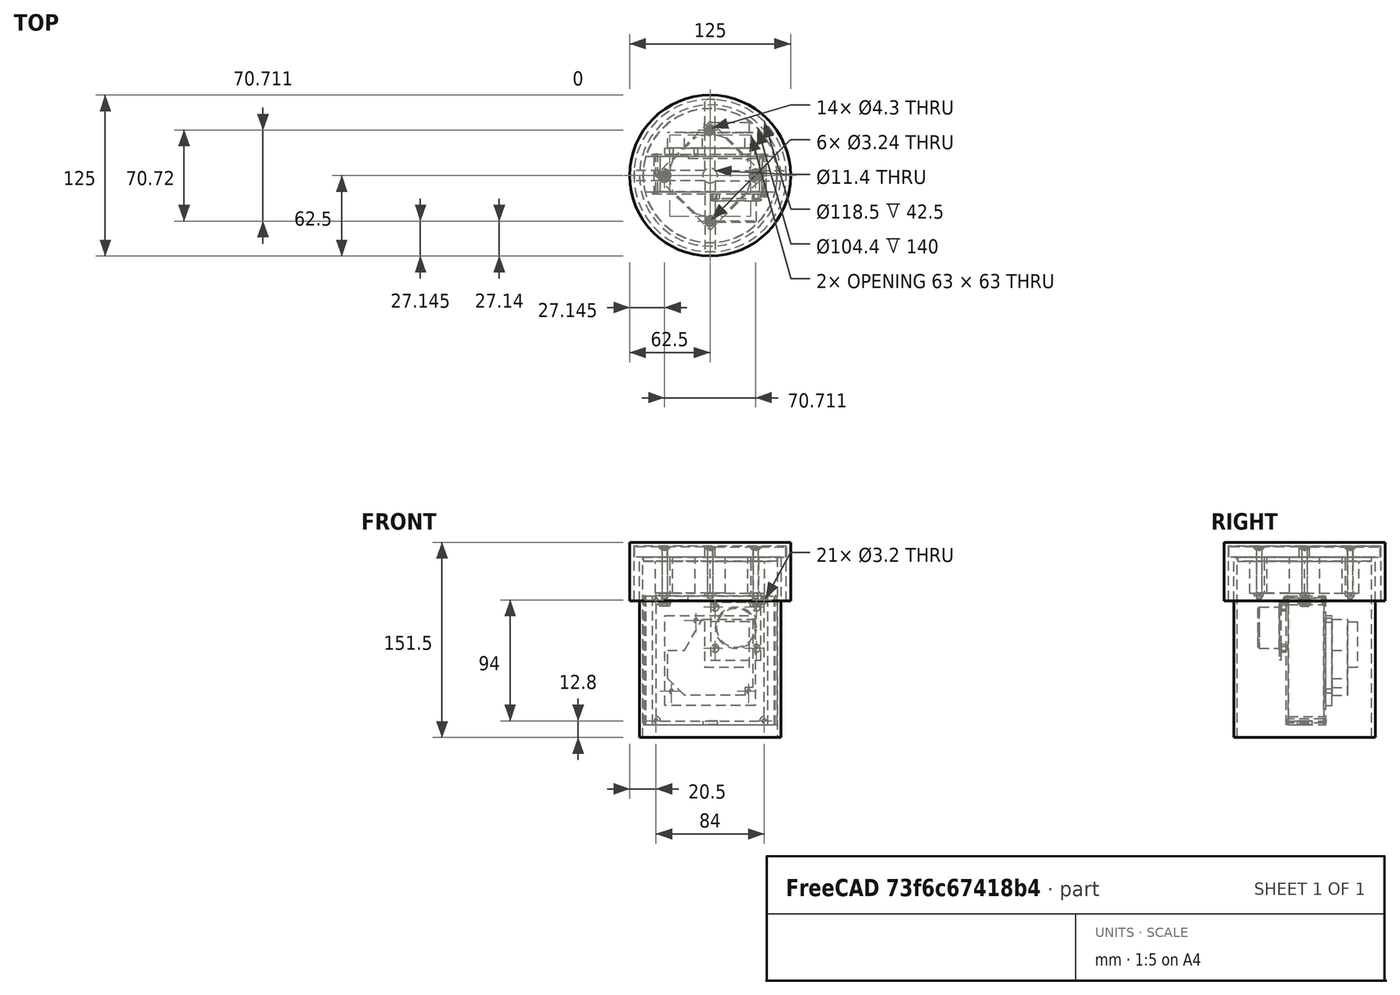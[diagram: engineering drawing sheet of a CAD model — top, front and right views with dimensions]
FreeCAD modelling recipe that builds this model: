
FCSTD DOCUMENT  (FreeCAD 0.18R16117 (Git))
Label: openair
License: All rights reserved
LicenseURL: http://en.wikipedia.org/wiki/All_rights_reserved
objects: Sketcher::SketchObject×20, PartDesign::Pad×15, Part::FeaturePython×14, PartDesign::Body×10, PartDesign::Pocket×5, Mesh::Feature×4, PartDesign::Chamfer×2
note: 86 computed .brp shape members not serialized (recipe doc carries the construction recipe); baked Part::Feature solids carry a one-line shape summary decoded from their .brp

FEATURE [Sketcher::SketchObject] Sketch002  label="tube_body_sketch"
  MapMode = 5
  Support = -> [XY_Plane001]
  sketch-geometry (2):
    g0: Circle CenterX=0 CenterY=0 CenterZ=0 NormalX=0 NormalY=0 NormalZ=1 AngleXU=0 Radius=54.9
    g1: Circle CenterX=0 CenterY=0 CenterZ=0 NormalX=0 NormalY=0 NormalZ=1 AngleXU=0 Radius=52.2
  constraints (4):
    c: Coincident(g0,g-1)
    c: Radius(g0) = 54.9  'tube_outer'
    c: Coincident(g1,g-1)
    c: Radius(g1) = 52.2  'tube_inner'
FEATURE [PartDesign::Pad] Pad001  label="tube_body"
  Length = 140
  Length2 = 100
  Profile = -> Sketch002
  Refine = true
  Reversed = true
  Type = 0
FEATURE [PartDesign::Body] Body001  label="tube"
  Group = -> [Sketch002,Pad001]
  Origin = -> Origin001
  Tip = -> Pad001
FEATURE [Sketcher::SketchObject] Sketch003  label="cross_body_sketch"
  MapMode = 5
  Support = -> [XY_Plane002]
  expr: Constraints[58] = fan_body_sketch.Constraints.hole_center_distance
  expr: Constraints[54] = fan_body_sketch.Constraints.fan_hole_radius
  expr: Constraints[48] = fan_body_sketch.Constraints.fan_hole_radius
  expr: Constraints[57] = fan_body_sketch.Constraints.hole_center_distance
  expr: Constraints[14] = Constraints.cross_width
  expr: Constraints[53] = fan_body_sketch.Constraints.fan_hole_radius
  expr: Constraints[55] = fan_body_sketch.Constraints.fan_hole_radius
  expr: Constraints[56] = fan_body_sketch.Constraints.hole_center_distance
  expr: Constraints[49] = fan_body_sketch.Constraints.hole_center_distance
  expr: Constraints[1] = cap_pocket_sketch.Constraints.cap_inner_radius - 0.2mm
  sketch-geometry (22):
    g0: Circle [constr] CenterX=0 CenterY=0 CenterZ=0 NormalX=0 NormalY=0 NormalZ=1 AngleXU=0 Radius=59.05
    g1: LineSegment [constr] StartX=-4 StartY=-4 StartZ=0 EndX=4 EndY=-4 EndZ=0
    g2: LineSegment [constr] StartX=4 StartY=-4 StartZ=0 EndX=4 EndY=4 EndZ=0
    g3: LineSegment [constr] StartX=4 StartY=4 StartZ=0 EndX=-4 EndY=4 EndZ=0
    g4: LineSegment [constr] StartX=-4 StartY=4 StartZ=0 EndX=-4 EndY=-4 EndZ=0
    g5: LineSegment [constr] StartX=-4 StartY=-4 StartZ=0 EndX=4 EndY=4 EndZ=0
    g6: LineSegment StartX=-4 StartY=4 StartZ=0 EndX=-58.9144 EndY=4 EndZ=0
    g7: LineSegment StartX=-4 StartY=-4 StartZ=0 EndX=-58.9144 EndY=-4 EndZ=0
    g8: LineSegment StartX=-4 StartY=4 StartZ=0 EndX=-4 EndY=58.9144 EndZ=0
    g9: LineSegment StartX=4 StartY=4 StartZ=0 EndX=4 EndY=58.9144 EndZ=0
    g10: LineSegment StartX=4 StartY=4 StartZ=0 EndX=58.9144 EndY=4 EndZ=0
    g11: LineSegment StartX=4 StartY=-4 StartZ=0 EndX=58.9144 EndY=-4 EndZ=0
    g12: LineSegment StartX=-4 StartY=-4 StartZ=0 EndX=-4 EndY=-58.9144 EndZ=0
    g13: LineSegment StartX=4 StartY=-4 StartZ=0 EndX=4 EndY=-58.9144 EndZ=0
    g14: ArcOfCircle CenterX=0 CenterY=0 CenterZ=0 NormalX=0 NormalY=0 NormalZ=1 AngleXU=0 Radius=59.05 StartAngle=4.6446 EndAngle=4.78018
    g15: ArcOfCircle CenterX=0 CenterY=0 CenterZ=0 NormalX=0 NormalY=0 NormalZ=1 AngleXU=0 Radius=59.05 StartAngle=3.0738 EndAngle=3.20938
    g16: ArcOfCircle CenterX=0 CenterY=0 CenterZ=0 NormalX=0 NormalY=0 NormalZ=1 AngleXU=0 Radius=59.05 StartAngle=1.50301 EndAngle=1.63859
    g17: ArcOfCircle CenterX=0 CenterY=0 CenterZ=0 NormalX=0 NormalY=0 NormalZ=1 AngleXU=0 Radius=59.05 StartAngle=6.21539 EndAngle=6.35098
    g18: Circle CenterX=0 CenterY=35.3553 CenterZ=0 NormalX=0 NormalY=0 NormalZ=1 AngleXU=0 Radius=2.15
    g19: Circle CenterX=-35.3553 CenterY=0 CenterZ=0 NormalX=0 NormalY=0 NormalZ=1 AngleXU=0 Radius=2.15
    g20: Circle CenterX=35.3553 CenterY=0 CenterZ=0 NormalX=0 NormalY=0 NormalZ=1 AngleXU=0 Radius=2.15
    g21: Circle CenterX=0 CenterY=-35.3553 CenterZ=0 NormalX=0 NormalY=0 NormalZ=1 AngleXU=0 Radius=2.15
  constraints (59):
    c: Coincident(g0,g-1)
    c: Radius(g0) = 59.05
    c: Coincident(g1,g2)
    c: Coincident(g2,g3)
    c: Coincident(g3,g4)
    c: Coincident(g4,g1)
    c: Horizontal(g1)
    c: Horizontal(g3)
    c: Vertical(g2)
    c: Vertical(g4)
    c: Coincident(g5,g1)
    c: Coincident(g5,g2)
    c: Symmetric(g5,g5,g-1)
    c: DistanceY(g2,g2) = 8  'cross_width'
    c: DistanceX(g3,g3) = 8
    c: Coincident(g6,g3)
    c: PointOnObject(g6,g0)
    c: Horizontal(g6)
    c: Coincident(g7,g1)
    c: Horizontal(g7)
    c: Coincident(g8,g3)
    c: PointOnObject(g8,g0)
    c: Vertical(g8)
    c: Coincident(g9,g2)
    c: Vertical(g9)
    c: Coincident(g10,g2)
    c: PointOnObject(g10,g0)
    c: Horizontal(g10)
    c: Coincident(g11,g1)
    c: Horizontal(g11)
    c: Coincident(g12,g1)
    c: PointOnObject(g12,g0)
    c: Vertical(g12)
    c: Coincident(g13,g1)
    c: Vertical(g13)
    c: Coincident(g14,g-1)
    c: Coincident(g14,g13)
    c: Coincident(g14,g12)
    c: Coincident(g15,g-1)
    c: Coincident(g15,g7)
    c: Coincident(g15,g6)
    c: Coincident(g16,g-1)
    c: Coincident(g16,g8)
    c: Coincident(g16,g9)
    c: Coincident(g17,g-1)
    c: Coincident(g17,g10)
    c: Coincident(g17,g11)
    c: PointOnObject(g18,g-2)
    c: Radius(g18) = 2.15
    c: Distance(g-1,g18) = 35.3553
    c: PointOnObject(g19,g-1)
    c: PointOnObject(g20,g-1)
    c: PointOnObject(g21,g-2)
    c: Radius(g19) = 2.15
    c: Radius(g20) = 2.15
    c: Radius(g21) = 2.15
    c: DistanceX(g19,g-1) = 35.3553
    c: DistanceX(g-1,g20) = 35.3553
    c: DistanceY(g21,g-1) = 35.3553
FEATURE [PartDesign::Pad] Pad002  label="cross_body"
  Length = 8
  Length2 = 100
  Profile = -> Sketch003
  Refine = true
  Type = 0
FEATURE [Sketcher::SketchObject] Sketch004  label="fan_body_sketch"
  MapMode = 5
  Support = -> [XY_Plane003]
  expr: Constraints[57] = Constraints.fan_hole_inset
  expr: Constraints[54] = Constraints.fan_hole_inset
  expr: Constraints[55] = Constraints.fan_hole_inset
  expr: Constraints[53] = Constraints.fan_hole_inset
  expr: Constraints[52] = Constraints.fan_hole_radius
  expr: Constraints[58] = Constraints.fan_hole_inset
  expr: Constraints[51] = Constraints.fan_hole_radius
  expr: Constraints[50] = Constraints.fan_hole_radius
  expr: Constraints[38] = Constraints.fan_cutout_radius
  expr: Constraints[49] = Constraints.fan_hole_inset
  expr: Constraints[37] = Constraints.fan_cutout_radius
  expr: Constraints[56] = Constraints.fan_hole_inset
  expr: Constraints[36] = Constraints.fan_cutout_radius
  expr: Constraints[22] = Constraints.fan_border_thickness
  expr: Constraints[21] = Constraints.fan_border_thickness
  expr: Constraints[20] = Constraints.fan_border_thickness
  expr: Constraints[10] = Constraints.fan_size
  sketch-geometry (20):
    g0: LineSegment StartX=-30 StartY=-30 StartZ=0 EndX=30 EndY=-30 EndZ=0
    g1: LineSegment StartX=30 StartY=-30 StartZ=0 EndX=30 EndY=30 EndZ=0
    g2: LineSegment StartX=30 StartY=30 StartZ=0 EndX=-30 EndY=30 EndZ=0
    g3: LineSegment StartX=-30 StartY=30 StartZ=0 EndX=-30 EndY=-30 EndZ=0
    g4: LineSegment [constr] StartX=-29 StartY=29 StartZ=0 EndX=29 EndY=29 EndZ=0
    g5: LineSegment [constr] StartX=29 StartY=29 StartZ=0 EndX=29 EndY=-29 EndZ=0
    g6: LineSegment [constr] StartX=29 StartY=-29 StartZ=0 EndX=-29 EndY=-29 EndZ=0
    g7: LineSegment [constr] StartX=-29 StartY=-29 StartZ=0 EndX=-29 EndY=29 EndZ=0
    g8: ArcOfCircle CenterX=0 CenterY=0 CenterZ=0 NormalX=0 NormalY=0 NormalZ=1 AngleXU=0 Radius=31.5 StartAngle=1.97189 EndAngle=2.7405
    g9: ArcOfCircle CenterX=0 CenterY=0 CenterZ=0 NormalX=0 NormalY=0 NormalZ=1 AngleXU=0 Radius=31.5 StartAngle=0.401093 EndAngle=1.1697
    g10: ArcOfCircle CenterX=0 CenterY=0 CenterZ=0 NormalX=0 NormalY=0 NormalZ=1 AngleXU=0 Radius=31.5 StartAngle=5.11348 EndAngle=5.88209
    g11: ArcOfCircle CenterX=0 CenterY=0 CenterZ=0 NormalX=0 NormalY=0 NormalZ=1 AngleXU=0 Radius=31.5 StartAngle=3.54269 EndAngle=4.3113
    g12: LineSegment StartX=-29 StartY=-12.2984 StartZ=0 EndX=-29 EndY=12.2984 EndZ=0
    g13: LineSegment StartX=-12.2984 StartY=29 StartZ=0 EndX=12.2984 EndY=29 EndZ=0
    g14: LineSegment StartX=29 StartY=12.2984 StartZ=0 EndX=29 EndY=-12.2984 EndZ=0
    g15: LineSegment StartX=12.2984 StartY=-29 StartZ=0 EndX=-12.2984 EndY=-29 EndZ=0
    g16: Circle CenterX=-25 CenterY=25 CenterZ=0 NormalX=0 NormalY=0 NormalZ=1 AngleXU=0 Radius=2.15
    g17: Circle CenterX=25 CenterY=25 CenterZ=0 NormalX=0 NormalY=0 NormalZ=1 AngleXU=0 Radius=2.15
    g18: Circle CenterX=25 CenterY=-25 CenterZ=0 NormalX=0 NormalY=0 NormalZ=1 AngleXU=0 Radius=2.15
    g19: Circle CenterX=-25 CenterY=-25 CenterZ=0 NormalX=0 NormalY=0 NormalZ=1 AngleXU=0 Radius=2.15
  constraints (60):
    c: Coincident(g0,g1)
    c: Coincident(g1,g2)
    c: Coincident(g2,g3)
    c: Coincident(g3,g0)
    c: Horizontal(g0)
    c: Horizontal(g2)
    c: Vertical(g1)
    c: Vertical(g3)
    c: Symmetric(g1,g0,g-1)
    c: Distance(g1) = 60  'fan_size'
    c: Distance(g0) = 60
    c: Coincident(g4,g5)
    c: Coincident(g5,g6)
    c: Coincident(g6,g7)
    c: Coincident(g7,g4)
    c: Horizontal(g4)
    c: Horizontal(g6)
    c: Vertical(g5)
    c: Vertical(g7)
    c: DistanceX(g2,g4) = 1  'fan_border_thickness'
    c: DistanceX(g4,g1) = 1
    c: DistanceY(g0,g6) = 1
    c: DistanceY(g4,g2) = 1
    c: Coincident(g8,g-1)
    c: PointOnObject(g8,g7)
    c: PointOnObject(g8,g4)
    c: Coincident(g9,g-1)
    c: PointOnObject(g9,g4)
    c: PointOnObject(g9,g5)
    c: Coincident(g10,g-1)
    c: PointOnObject(g10,g5)
    c: PointOnObject(g10,g6)
    c: Coincident(g11,g-1)
    c: PointOnObject(g11,g6)
    c: PointOnObject(g11,g7)
    c: Radius(g8) = 31.5  'fan_cutout_radius'
    c: Radius(g9) = 31.5
    c: Radius(g10) = 31.5
    c: Radius(g11) = 31.5
    c: Coincident(g12,g11)
    c: Coincident(g12,g8)
    c: Coincident(g13,g8)
    c: Coincident(g13,g9)
    c: Coincident(g14,g9)
    c: Coincident(g14,g10)
    c: Coincident(g15,g10)
    c: Coincident(g15,g11)
    c: Radius(g16) = 2.15  'fan_hole_radius'
    c: DistanceX(g2,g16) = 5  'fan_hole_inset'
    c: DistanceY(g16,g2) = 5
    c: Radius(g17) = 2.15
    c: Radius(g18) = 2.15
    c: Radius(g19) = 2.15
    c: DistanceX(g0,g19) = 5
    c: DistanceX(g18,g0) = 5
    c: DistanceX(g17,g1) = 5
    c: DistanceY(g17,g1) = 5
    c: DistanceY(g0,g18) = 5
    c: DistanceY(g0,g19) = 5
    c: Distance(g17,g-1) = 35.3553  'hole_center_distance'
FEATURE [PartDesign::Pad] Pad003  label="fan_body"
  Length = 25
  Length2 = 100
  Profile = -> Sketch004
  Refine = true
  Type = 0
FEATURE [PartDesign::Body] Body003  label="fan"
  Group = -> [Sketch004,Pad003]
  Origin = -> Origin003
  Placement = pos=(0,0,-28) rot=(0,0,1;0.785398rad)
  Tip = -> Pad003
FEATURE [PartDesign::Chamfer] Chamfer  label="cross_countersink"
  Base = -> Pad002 [Edge48,Edge45,Edge39,Edge42]
  BaseFeature = -> Pad002
  Size = 1.61
FEATURE [PartDesign::Body] Body002  label="cross"
  Group = -> [Sketch003,Pad002,Chamfer]
  Origin = -> Origin002
  Tip = -> Chamfer
FEATURE [Sketcher::SketchObject] Sketch005  label="plate_sketch"
  MapMode = 5
  Support = -> [XY_Plane005]
  expr: Constraints[52] = fan_body_sketch.Constraints.fan_hole_radius
  expr: Constraints[51] = fan_body_sketch.Constraints.fan_hole_radius
  expr: Constraints[48] = fan_body_sketch.Constraints.hole_center_distance
  expr: Constraints[49] = fan_body_sketch.Constraints.fan_hole_radius
  expr: Constraints[47] = fan_body_sketch.Constraints.hole_center_distance
  expr: Constraints[50] = fan_body_sketch.Constraints.fan_hole_radius
  expr: Constraints[46] = fan_body_sketch.Constraints.hole_center_distance
  expr: Constraints[45] = fan_body_sketch.Constraints.hole_center_distance
  expr: Constraints[27] = fan_body_sketch.Constraints.fan_cutout_radius
  expr: Constraints[28] = fan_body_sketch.Constraints.fan_cutout_radius
  expr: Constraints[26] = fan_body_sketch.Constraints.fan_cutout_radius
  expr: Constraints[25] = fan_body_sketch.Constraints.fan_cutout_radius
  expr: Constraints[12] = fan_body_sketch.Constraints.fan_size - 2 * fan_body_sketch.Constraints.fan_border_thickness
  expr: Constraints[11] = fan_body_sketch.Constraints.fan_size - 2 * fan_body_sketch.Constraints.fan_border_thickness
  expr: Constraints.diameter = tube_body_sketch.Constraints.tube_inner - 0.2mm
  sketch-geometry (19):
    g0: Circle CenterX=0 CenterY=0 CenterZ=0 NormalX=0 NormalY=0 NormalZ=1 AngleXU=0 Radius=52
    g1: LineSegment [constr] StartX=-29 StartY=29 StartZ=0 EndX=29 EndY=29 EndZ=0
    g2: LineSegment [constr] StartX=29 StartY=29 StartZ=0 EndX=29 EndY=-29 EndZ=0
    g3: LineSegment [constr] StartX=29 StartY=-29 StartZ=0 EndX=-29 EndY=-29 EndZ=0
    g4: LineSegment [constr] StartX=-29 StartY=-29 StartZ=0 EndX=-29 EndY=29 EndZ=0
    g5: ArcOfCircle CenterX=0 CenterY=0 CenterZ=0 NormalX=0 NormalY=0 NormalZ=1 AngleXU=0 Radius=31.5 StartAngle=1.97189 EndAngle=2.7405
    g6: ArcOfCircle CenterX=0 CenterY=0 CenterZ=0 NormalX=0 NormalY=0 NormalZ=1 AngleXU=0 Radius=31.5 StartAngle=0.401093 EndAngle=1.1697
    g7: ArcOfCircle CenterX=0 CenterY=0 CenterZ=0 NormalX=0 NormalY=0 NormalZ=1 AngleXU=0 Radius=31.5 StartAngle=5.11348 EndAngle=5.88209
    g8: ArcOfCircle CenterX=0 CenterY=0 CenterZ=0 NormalX=0 NormalY=0 NormalZ=1 AngleXU=0 Radius=31.5 StartAngle=3.54269 EndAngle=4.3113
    g9: LineSegment StartX=-29 StartY=-12.2984 StartZ=0 EndX=-29 EndY=12.2984 EndZ=0
    g10: LineSegment StartX=-12.2984 StartY=29 StartZ=0 EndX=12.2984 EndY=29 EndZ=0
    g11: LineSegment StartX=29 StartY=12.2984 StartZ=0 EndX=29 EndY=-12.2984 EndZ=0
    g12: LineSegment StartX=12.2984 StartY=-29 StartZ=0 EndX=-12.2984 EndY=-29 EndZ=0
    g13: LineSegment [constr] StartX=-29 StartY=29 StartZ=0 EndX=29 EndY=-29 EndZ=0
    g14: LineSegment [constr] StartX=29 StartY=29 StartZ=0 EndX=-29 EndY=-29 EndZ=0
    g15: Circle CenterX=-25 CenterY=25 CenterZ=0 NormalX=0 NormalY=0 NormalZ=1 AngleXU=0 Radius=2.15
    g16: Circle CenterX=25 CenterY=25 CenterZ=0 NormalX=0 NormalY=0 NormalZ=1 AngleXU=0 Radius=2.15
    g17: Circle CenterX=25 CenterY=-25 CenterZ=0 NormalX=0 NormalY=0 NormalZ=1 AngleXU=0 Radius=2.15
    g18: Circle CenterX=-25 CenterY=-25 CenterZ=0 NormalX=0 NormalY=0 NormalZ=1 AngleXU=0 Radius=2.15
  constraints (53):
    c: Coincident(g0,g-1)
    c: Radius(g0) = 52  'diameter'
    c: Coincident(g1,g2)
    c: Coincident(g2,g3)
    c: Coincident(g3,g4)
    c: Coincident(g4,g1)
    c: Horizontal(g1)
    c: Horizontal(g3)
    c: Vertical(g2)
    c: Vertical(g4)
    c: Symmetric(g3,g1,g-1)
    c: Distance(g1) = 58
    c: Distance(g4) = 58
    c: Coincident(g5,g-1)
    c: PointOnObject(g5,g4)
    c: PointOnObject(g5,g1)
    c: Coincident(g6,g-1)
    c: PointOnObject(g6,g1)
    c: PointOnObject(g6,g2)
    c: Coincident(g7,g-1)
    c: PointOnObject(g7,g2)
    c: PointOnObject(g7,g3)
    c: Coincident(g8,g-1)
    c: PointOnObject(g8,g3)
    c: PointOnObject(g8,g4)
    c: Radius(g5) = 31.5
    c: Radius(g6) = 31.5
    c: Radius(g7) = 31.5
    c: Radius(g8) = 31.5
    c: Coincident(g9,g8)
    c: Coincident(g9,g5)
    c: Coincident(g10,g5)
    c: Coincident(g10,g6)
    c: Coincident(g11,g6)
    c: Coincident(g11,g7)
    c: Coincident(g12,g7)
    c: Coincident(g12,g8)
    c: Coincident(g13,g1)
    c: Coincident(g13,g2)
    c: Coincident(g14,g1)
    c: Coincident(g14,g3)
    c: PointOnObject(g15,g13)
    c: PointOnObject(g16,g14)
    c: PointOnObject(g17,g13)
    c: PointOnObject(g18,g14)
    c: Distance(g15,g-1) = 35.3553
    c: Distance(g16,g-1) = 35.3553
    c: Distance(g17,g-1) = 35.3553
    c: Distance(g-1,g18) = 35.3553
    c: Radius(g15) = 2.15
    c: Radius(g16) = 2.15
    c: Radius(g18) = 2.15
    c: Radius(g17) = 2.15
FEATURE [PartDesign::Pad] Pad004  label="plate_body"
  Length = 3
  Length2 = 100
  Profile = -> Sketch005
  Refine = true
  Type = 0
FEATURE [PartDesign::Body] Body005  label="plate"
  Group = -> [Sketch005,Pad004]
  Origin = -> Origin005
  Placement = pos=(0,0,-3) rot=(0,0,1;0.785398rad)
  Tip = -> Pad004
FEATURE [Sketcher::SketchObject] Sketch006  label="housing_body_sketch"
  MapMode = 5
  Support = -> [XY_Plane006]
  expr: Constraints[1] = tube_body_sketch.Constraints.tube_inner - 0.2mm
  sketch-geometry (5):
    g0: Circle [constr] CenterX=0 CenterY=0 CenterZ=0 NormalX=0 NormalY=0 NormalZ=1 AngleXU=0 Radius=52
    g1: LineSegment StartX=-49.7896 StartY=15 StartZ=0 EndX=49.7896 EndY=15 EndZ=0
    g2: LineSegment StartX=-50.4752 StartY=-12.5 StartZ=0 EndX=50.4752 EndY=-12.5 EndZ=0
    g3: ArcOfCircle CenterX=0 CenterY=0 CenterZ=0 NormalX=0 NormalY=0 NormalZ=1 AngleXU=0 Radius=52 StartAngle=6.04042 EndAngle=6.5758
    g4: ArcOfCircle CenterX=0 CenterY=0 CenterZ=0 NormalX=0 NormalY=0 NormalZ=1 AngleXU=0 Radius=52 StartAngle=2.84897 EndAngle=3.38435
  constraints (14):
    c: Coincident(g0,g-1)
    c: Radius(g0) = 52
    c: Horizontal(g1)
    c: Horizontal(g2)
    c: Coincident(g3,g-1)
    c: Coincident(g3,g1)
    c: Coincident(g3,g2)
    c: Coincident(g4,g-1)
    c: Coincident(g4,g2)
    c: Coincident(g4,g1)
    c: DistanceY(g3,g1) = 15  'housing_depth_back'
    c: DistanceY(g2,g3) = 12.5  'housing_depth_front'
    c: Equal(g3,g0)
    c: Equal(g4,g0)
FEATURE [PartDesign::Pad] Pad005  label="housing_body"
  Length = 100
  Length2 = 100
  Profile = -> Sketch006
  Refine = true
  Type = 0
FEATURE [Sketcher::SketchObject] Sketch007  label="housing_cutouts_sketch"
  ExternalGeometry = -> [Pad005]
  MapMode = 5
  Placement = pos=(0,-12.5,0) rot=(1,0,0;1.5708rad)
  Support = -> [Pad005]
  expr: Constraints[61] = Constraints.housing_hole_keep_radius
  expr: Constraints[60] = Constraints.housing_hole_keep_radius
  expr: Constraints[43] = Constraints.housing_hole_radius
  expr: Constraints[42] = Constraints.housing_hole_radius
  expr: Constraints[59] = Constraints.housing_hole_keep_radius
  expr: Constraints[49] = Constraints.housing_hole_radius
  expr: Constraints[37] = Constraints.cutout_inset
  expr: Constraints[36] = Constraints.module_hole_inset
  expr: Constraints[24] = Constraints.cutout_inset
  expr: Constraints[35] = Constraints.module_hole_inset
  expr: Constraints[23] = Constraints.cutout_inset
  expr: Constraints[34] = Constraints.module_hole_inset
  sketch-geometry (26):
    g0: LineSegment [constr] StartX=-45 StartY=100 StartZ=0 EndX=45 EndY=100 EndZ=0
    g1: LineSegment [constr] StartX=45 StartY=100 StartZ=0 EndX=45 EndY=0 EndZ=0
    g2: LineSegment [constr] StartX=45 StartY=0 StartZ=0 EndX=-45 EndY=0 EndZ=0
    g3: LineSegment [constr] StartX=-45 StartY=0 StartZ=0 EndX=-45 EndY=100 EndZ=0
    g4: LineSegment [constr] StartX=-50.4752 StartY=100 StartZ=0 EndX=50.4752 EndY=0 EndZ=0
    g5: GeomPoint X=0 Y=50 Z=0
    g6: LineSegment [constr] StartX=-44 StartY=99 StartZ=0 EndX=44 EndY=99 EndZ=0
    g7: LineSegment [constr] StartX=44 StartY=99 StartZ=0 EndX=44 EndY=1 EndZ=0
    g8: LineSegment [constr] StartX=44 StartY=1 StartZ=0 EndX=-44 EndY=1 EndZ=0
    g9: LineSegment [constr] StartX=-44 StartY=1 StartZ=0 EndX=-44 EndY=99 EndZ=0
    g10: LineSegment [constr] StartX=-42 StartY=97 StartZ=0 EndX=42 EndY=97 EndZ=0
    g11: LineSegment [constr] StartX=42 StartY=97 StartZ=0 EndX=42 EndY=3 EndZ=0
    g12: LineSegment [constr] StartX=42 StartY=3 StartZ=0 EndX=-42 EndY=3 EndZ=0
    g13: LineSegment [constr] StartX=-42 StartY=3 StartZ=0 EndX=-42 EndY=97 EndZ=0
    g14: Circle CenterX=-42 CenterY=97 CenterZ=0 NormalX=0 NormalY=0 NormalZ=1 AngleXU=0 Radius=1.6
    g15: Circle CenterX=42 CenterY=97 CenterZ=0 NormalX=0 NormalY=0 NormalZ=1 AngleXU=0 Radius=1.6
    g16: Circle CenterX=42 CenterY=3 CenterZ=0 NormalX=0 NormalY=0 NormalZ=1 AngleXU=0 Radius=1.6
    g17: ArcOfCircle CenterX=-42 CenterY=97 CenterZ=0 NormalX=0 NormalY=0 NormalZ=1 AngleXU=0 Radius=3.5 StartAngle=4.71239 EndAngle=6.28319
    g18: Circle CenterX=-42 CenterY=3 CenterZ=0 NormalX=0 NormalY=0 NormalZ=1 AngleXU=0 Radius=1.6
    g19: ArcOfCircle CenterX=42 CenterY=97 CenterZ=0 NormalX=0 NormalY=0 NormalZ=1 AngleXU=0 Radius=3.5 StartAngle=3.14159 EndAngle=4.71239
    g20: ArcOfCircle CenterX=42 CenterY=3 CenterZ=0 NormalX=0 NormalY=0 NormalZ=1 AngleXU=0 Radius=3.5 StartAngle=1.5708 EndAngle=3.14159
    g21: ArcOfCircle CenterX=-42 CenterY=3 CenterZ=0 NormalX=0 NormalY=0 NormalZ=1 AngleXU=0 Radius=3.5 StartAngle=0 EndAngle=1.5708
    g22: LineSegment StartX=-42 StartY=6.5 StartZ=0 EndX=-42 EndY=93.5 EndZ=0
    g23: LineSegment StartX=-38.5 StartY=97 StartZ=0 EndX=38.5 EndY=97 EndZ=0
    g24: LineSegment StartX=42 StartY=93.5 StartZ=0 EndX=42 EndY=6.5 EndZ=0
    g25: LineSegment StartX=38.5 StartY=3 StartZ=0 EndX=-38.5 EndY=3 EndZ=0
  constraints (70):
    c: Coincident(g0,g1)
    c: Coincident(g1,g2)
    c: Coincident(g2,g3)
    c: Coincident(g3,g0)
    c: Horizontal(g0)
    c: Horizontal(g2)
    c: Vertical(g1)
    c: Vertical(g3)
    c: Coincident(g4,g-3)
    c: Coincident(g4,g-4)
    c: Symmetric(g4,g4,g5)
    c: Symmetric(g2,g0,g5)
    c: DistanceX(g0,g0) = 90  'module_width'
    c: DistanceY(g1,g1) = 100  'module_height'
    c: Coincident(g6,g7)
    c: Coincident(g7,g8)
    c: Coincident(g8,g9)
    c: Coincident(g9,g6)
    c: Horizontal(g6)
    c: Horizontal(g8)
    c: Vertical(g7)
    c: Vertical(g9)
    c: DistanceX(g0,g6) = 1  'cutout_inset'
    c: DistanceY(g6,g0) = 1
    c: DistanceY(g1,g7) = 1
    c: Coincident(g10,g11)
    c: Coincident(g11,g12)
    c: Coincident(g12,g13)
    c: Coincident(g13,g10)
    c: Horizontal(g10)
    c: Horizontal(g12)
    c: Vertical(g11)
    c: Vertical(g13)
    c: DistanceX(g0,g10) = 3  'module_hole_inset'
    c: DistanceY(g10,g0) = 3
    c: DistanceX(g11,g1) = 3
    c: DistanceY(g1,g11) = 3
    c: DistanceX(g7,g1) = 1
    c: Coincident(g14,g10)
    c: Coincident(g15,g10)
    c: Coincident(g16,g11)
    c: Radius(g15) = 1.6  'housing_hole_radius'
    c: Radius(g16) = 1.6
    c: Radius(g14) = 1.6
    c: Coincident(g17,g10)
    c: PointOnObject(g17,g13)
    c: PointOnObject(g17,g10)
    c: Radius(g17) = 3.5  'housing_hole_keep_radius'
    c: Coincident(g18,g12)
    c: Radius(g18) = 1.6
    c: Coincident(g19,g10)
    c: PointOnObject(g19,g10)
    c: PointOnObject(g19,g11)
    c: Coincident(g20,g11)
    c: PointOnObject(g20,g11)
    c: PointOnObject(g20,g12)
    c: Coincident(g21,g12)
    c: PointOnObject(g21,g12)
    c: PointOnObject(g21,g13)
    c: Radius(g21) = 3.5
    c: Radius(g20) = 3.5
    c: Radius(g19) = 3.5
    c: Coincident(g22,g21)
    c: Coincident(g22,g17)
    c: Coincident(g23,g17)
    c: Coincident(g23,g19)
    c: Coincident(g24,g19)
    c: Coincident(g24,g20)
    c: Coincident(g25,g20)
    c: Coincident(g25,g21)
FEATURE [PartDesign::Pocket] Pocket001  label="housing_cutouts_body"
  BaseFeature = -> Pad005
  Length = 5
  Length2 = 100
  Profile = -> Sketch007
  Refine = true
  Type = 1
FEATURE [Sketcher::SketchObject] Sketch008  label="housing_cutouts_top_sketch"
  MapMode = 5
  Placement = pos=(0,0,100) rot=(0,0,1;0rad)
  Support = -> [Pocket001]
  expr: Constraints[5] = fan_body_sketch.Constraints.hole_center_distance
  expr: Constraints[4] = fan_body_sketch.Constraints.hole_center_distance
  expr: Constraints[2] = fan_body_sketch.Constraints.fan_hole_radius
  sketch-geometry (2):
    g0: Circle CenterX=-35.3553 CenterY=0 CenterZ=0 NormalX=0 NormalY=0 NormalZ=1 AngleXU=0 Radius=2.15
    g1: Circle CenterX=35.3553 CenterY=0 CenterZ=0 NormalX=0 NormalY=0 NormalZ=1 AngleXU=0 Radius=2.15
  constraints (6):
    c: PointOnObject(g0,g-1)
    c: PointOnObject(g1,g-1)
    c: Radius(g0) = 2.15
    c: Equal(g0,g1)
    c: DistanceX(g0,g-1) = 35.3553
    c: DistanceX(g-1,g1) = 35.3553
FEATURE [PartDesign::Pocket] Pocket002  label="housing_cutouts_top"
  BaseFeature = -> Pocket001
  Length = 50
  Length2 = 100
  Profile = -> Sketch008
  Refine = true
  Type = 0
FEATURE [Part::FeaturePython] Screw  label="M4x40-Screw"  # Fasteners workbench fastener (typed FeaturePython)
  Placement = pos=(35.3553,0,8) rot=(0,0,1;0rad)
  diameter = 6
  invert = false
  length = 11
  matchOuter = false
  offset = 0
  thread = false
  type = 17
FEATURE [Part::FeaturePython] Screw001  label="M4x40-Screw001"  # Fasteners workbench fastener (typed FeaturePython)
  Placement = pos=(-35.3553,0,8) rot=(0,0,1;0rad)
  diameter = 6
  invert = false
  length = 11
  matchOuter = false
  offset = 0
  thread = false
  type = 17
FEATURE [Part::FeaturePython] Nut  label="M4-Nut012"  # Fasteners workbench fastener (typed FeaturePython)
  Placement = pos=(-35.3553,0,-30.2) rot=(0,0,1;0rad)
  diameter = 6
  invert = false
  matchOuter = false
  offset = 0
  thread = false
  type = 6
FEATURE [Part::FeaturePython] Nut001  label="M4-Nut"  # Fasteners workbench fastener (typed FeaturePython)
  Placement = pos=(35.3553,0,-30.2) rot=(0,0,1;0rad)
  diameter = 6
  invert = false
  matchOuter = false
  offset = 0
  thread = false
  type = 6
FEATURE [Part::FeaturePython] Nut002  label="M4-Nut018"  # Fasteners workbench fastener (typed FeaturePython)
  Placement = pos=(35.3553,0,-37.9) rot=(0,0,1;0rad)
  diameter = 6
  invert = false
  matchOuter = false
  offset = 0
  thread = false
  type = 6
FEATURE [Part::FeaturePython] Nut003  label="M4-Nut017"  # Fasteners workbench fastener (typed FeaturePython)
  Placement = pos=(-35.3553,0,-37.9) rot=(0,0,1;0rad)
  diameter = 6
  invert = false
  matchOuter = false
  offset = 0
  thread = false
  type = 6
FEATURE [Part::FeaturePython] Screw002  label="M4x40-Screw003"  # Fasteners workbench fastener (typed FeaturePython)
  Placement = pos=(0,35.36,8) rot=(0,0,1;0rad)
  diameter = 6
  invert = false
  length = 11
  matchOuter = false
  offset = 0
  thread = false
  type = 17
FEATURE [Part::FeaturePython] Screw003  label="M4x40-Screw002"  # Fasteners workbench fastener (typed FeaturePython)
  Placement = pos=(0,-35.36,8) rot=(0,0,1;0rad)
  diameter = 6
  invert = false
  length = 11
  matchOuter = false
  offset = 0
  thread = false
  type = 17
FEATURE [Part::FeaturePython] Nut004  label="M4-Nut015"  # Fasteners workbench fastener (typed FeaturePython)
  Placement = pos=(0,-35.36,-30.2) rot=(0,0,1;0rad)
  diameter = 6
  invert = false
  matchOuter = false
  offset = 0
  thread = false
  type = 6
FEATURE [Part::FeaturePython] Nut005  label="M4-Nut016"  # Fasteners workbench fastener (typed FeaturePython)
  Placement = pos=(0,35.36,-30.2) rot=(0,0,1;0rad)
  diameter = 6
  invert = false
  matchOuter = false
  offset = 0
  thread = false
  type = 6
FEATURE [Sketcher::SketchObject] Sketch009  label="cap_body_sketch"
  MapMode = 5
  Support = -> [XY_Plane007]
  sketch-geometry (1):
    g0: Circle CenterX=0 CenterY=0 CenterZ=0 NormalX=0 NormalY=0 NormalZ=1 AngleXU=0 Radius=62.5
  constraints (2):
    c: Coincident(g0,g-1)
    c: Radius(g0) = 62.5  'cap_outer_radius'
FEATURE [PartDesign::Pad] Pad006  label="cap_body"
  Length = 45.5
  Length2 = 100
  Profile = -> Sketch009
  Refine = true
  Type = 0
FEATURE [Sketcher::SketchObject] Sketch010  label="cap_pocket_sketch"
  MapMode = 5
  Placement = pos=(0,0,0) rot=(1,0,0;3.14159rad)
  Support = -> [Pad006]
  sketch-geometry (1):
    g0: Circle CenterX=0 CenterY=0 CenterZ=0 NormalX=0 NormalY=0 NormalZ=1 AngleXU=0 Radius=59.25
  constraints (2):
    c: Coincident(g0,g-1)
    c: Radius(g0) = 59.25  'cap_inner_radius'
FEATURE [PartDesign::Pocket] Pocket003  label="cap_pocket"
  BaseFeature = -> Pad006
  Length = 42.5
  Length2 = 100
  Profile = -> Sketch010
  Refine = true
  Type = 0
  expr: Length = cap_body.Length - 3mm
FEATURE [PartDesign::Body] Body007  label="cap"
  Group = -> [Sketch009,Pad006,Sketch010,Pocket003]
  Origin = -> Origin007
  Placement = pos=(0,0,-34) rot=(0,0,1;0rad)
  Tip = -> Pocket003
FEATURE [Sketcher::SketchObject] Sketch  label="gasmod-base-sketch"
  MapMode = 5
  Placement = pos=(0,0,0) rot=(1,0,0;1.5708rad)
  Support = -> [XZ_Plane]
  expr: Constraints[22] = housing_cutouts_sketch.Constraints.module_hole_inset
  expr: Constraints[21] = housing_cutouts_sketch.Constraints.module_hole_inset
  expr: Constraints[20] = housing_cutouts_sketch.Constraints.module_hole_inset
  expr: Constraints[19] = housing_cutouts_sketch.Constraints.module_hole_inset
  expr: Constraints[10] = housing_cutouts_sketch.Constraints.module_height
  expr: Constraints[9] = housing_cutouts_sketch.Constraints.module_width
  sketch-geometry (12):
    g0: LineSegment StartX=-45 StartY=-50 StartZ=0 EndX=45 EndY=-50 EndZ=0
    g1: LineSegment StartX=45 StartY=-50 StartZ=0 EndX=45 EndY=50 EndZ=0
    g2: LineSegment StartX=45 StartY=50 StartZ=0 EndX=-45 EndY=50 EndZ=0
    g3: LineSegment StartX=-45 StartY=50 StartZ=0 EndX=-45 EndY=-50 EndZ=0
    g4: LineSegment [constr] StartX=-42 StartY=47 StartZ=0 EndX=42 EndY=47 EndZ=0
    g5: LineSegment [constr] StartX=42 StartY=47 StartZ=0 EndX=42 EndY=-47 EndZ=0
    g6: LineSegment [constr] StartX=42 StartY=-47 StartZ=0 EndX=-42 EndY=-47 EndZ=0
    g7: LineSegment [constr] StartX=-42 StartY=-47 StartZ=0 EndX=-42 EndY=47 EndZ=0
    g8: Circle CenterX=-42 CenterY=47 CenterZ=0 NormalX=0 NormalY=0 NormalZ=1 AngleXU=0 Radius=1.6
    g9: Circle CenterX=42 CenterY=47 CenterZ=0 NormalX=0 NormalY=0 NormalZ=1 AngleXU=0 Radius=1.6
    g10: Circle CenterX=-42 CenterY=-47 CenterZ=0 NormalX=0 NormalY=0 NormalZ=1 AngleXU=0 Radius=1.6
    g11: Circle CenterX=42 CenterY=-47 CenterZ=0 NormalX=0 NormalY=0 NormalZ=1 AngleXU=0 Radius=1.6
  constraints (31):
    c: Coincident(g0,g1)
    c: Coincident(g1,g2)
    c: Coincident(g2,g3)
    c: Coincident(g3,g0)
    c: Horizontal(g0)
    c: Horizontal(g2)
    c: Vertical(g1)
    c: Vertical(g3)
    c: Symmetric(g0,g1,g-1)
    c: DistanceX(g2,g2) = 90
    c: DistanceY(g1,g1) = 100
    c: Coincident(g4,g5)
    c: Coincident(g5,g6)
    c: Coincident(g6,g7)
    c: Coincident(g7,g4)
    c: Horizontal(g4)
    c: Horizontal(g6)
    c: Vertical(g5)
    c: Vertical(g7)
    c: DistanceX(g2,g4) = 3
    c: DistanceX(g5,g0) = 3
    c: DistanceY(g4,g2) = 3
    c: DistanceY(g0,g5) = 3
    c: Coincident(g9,g4)
    c: Coincident(g10,g6)
    c: Coincident(g11,g5)
    c: Equal(g8,g9)
    c: Equal(g9,g11)
    c: Equal(g11,g10)
    c: Radius(g8) = 1.6
    c: Coincident(g4,g8)
FEATURE [PartDesign::Pad] Pad  label="gasmod-base"
  Length = 1.6
  Length2 = 100
  Placement = pos=(0,0,0) rot=(1,0,0;1.5708rad)
  Profile = -> Sketch
  Refine = true
  Type = 0
FEATURE [PartDesign::Body] Body  label="gasmod"
  Group = -> [Sketch,Pad]
  Origin = -> Origin
  Placement = pos=(0,-12.5,-80.2) rot=(0,0,1;0rad)
  Tip = -> Pad
  expr: Placement.Base.y = -housing_body_sketch.Constraints.housing_depth_front
FEATURE [Sketcher::SketchObject] Sketch011  label="isb_base_sketch"
  MapMode = 5
  Placement = pos=(0,0,0) rot=(1,0,0;1.5708rad)
  Support = -> [XZ_Plane008]
  expr: Constraints[18] = Constraints.isb_hole_inset
  expr: Constraints[20] = Constraints.isb_hole_dist
  sketch-geometry (13):
    g0: LineSegment StartX=-19.55 StartY=-22.3 StartZ=0 EndX=19.55 EndY=-22.3 EndZ=0
    g1: LineSegment StartX=19.55 StartY=-22.3 StartZ=0 EndX=19.55 EndY=22.3 EndZ=0
    g2: LineSegment StartX=19.55 StartY=22.3 StartZ=0 EndX=-19.55 EndY=22.3 EndZ=0
    g3: LineSegment StartX=-19.55 StartY=22.3 StartZ=0 EndX=-19.55 EndY=-22.3 EndZ=0
    g4: LineSegment [constr] StartX=-15.95 StartY=13.3 StartZ=0 EndX=16.05 EndY=13.3 EndZ=0
    g5: LineSegment [constr] StartX=16.05 StartY=13.3 StartZ=0 EndX=16.05 EndY=-18.7 EndZ=0
    g6: LineSegment [constr] StartX=16.05 StartY=-18.7 StartZ=0 EndX=-15.95 EndY=-18.7 EndZ=0
    g7: LineSegment [constr] StartX=-15.95 StartY=-18.7 StartZ=0 EndX=-15.95 EndY=13.3 EndZ=0
    g8: Circle [constr] CenterX=-15.95 CenterY=13.3 CenterZ=0 NormalX=0 NormalY=0 NormalZ=1 AngleXU=0 Radius=0
    g9: Circle CenterX=-15.95 CenterY=13.3 CenterZ=0 NormalX=0 NormalY=0 NormalZ=1 AngleXU=0 Radius=1.6
    g10: Circle CenterX=16.05 CenterY=13.3 CenterZ=0 NormalX=0 NormalY=0 NormalZ=1 AngleXU=0 Radius=1.6
    g11: Circle CenterX=16.05 CenterY=-18.7 CenterZ=0 NormalX=0 NormalY=0 NormalZ=1 AngleXU=0 Radius=1.6
    g12: Circle CenterX=-15.95 CenterY=-18.7 CenterZ=0 NormalX=0 NormalY=0 NormalZ=1 AngleXU=0 Radius=1.6
  constraints (33):
    c: Coincident(g0,g1)
    c: Coincident(g1,g2)
    c: Coincident(g2,g3)
    c: Coincident(g3,g0)
    c: Horizontal(g0)
    c: Horizontal(g2)
    c: Vertical(g1)
    c: Vertical(g3)
    c: Symmetric(g0,g1,g-1)
    c: DistanceX(g0,g0) = 39.1
    c: Coincident(g4,g5)
    c: Coincident(g5,g6)
    c: Coincident(g6,g7)
    c: Coincident(g7,g4)
    c: Horizontal(g4)
    c: Horizontal(g6)
    c: Vertical(g5)
    c: Vertical(g7)
    c: DistanceX(g0,g6) = 3.6
    c: DistanceY(g0,g6) = 3.6  'isb_hole_inset'
    c: DistanceX(g6,g6) = 32
    c: DistanceY(g3,g3) = 44.6  'isb_height'
    c: DistanceY(g7,g7) = 32  'isb_hole_dist'
    c: Coincident(g8,g4)
    c: Tangent(g8,g4)
    c: Coincident(g9,g4)
    c: Coincident(g10,g4)
    c: Coincident(g11,g5)
    c: Coincident(g12,g6)
    c: Equal(g9,g10)
    c: Equal(g10,g11)
    c: Equal(g11,g12)
    c: Radius(g9) = 1.6
FEATURE [PartDesign::Pad] Pad007  label="isb_base"
  Length = 1.6
  Length2 = 100
  Placement = pos=(0,0,0) rot=(1,0,0;1.5708rad)
  Profile = -> Sketch011
  Refine = true
  Type = 0
FEATURE [Sketcher::SketchObject] Sketch012  label="isb_sensor_sketch"
  ExternalGeometry = -> [Pad007]
  MapMode = 5
  Placement = pos=(0,-1.6,7e-16) rot=(1,0,0;1.5708rad)
  Support = -> [Pad007]
  sketch-geometry (1):
    g0: Circle CenterX=0 CenterY=-2.7 CenterZ=0 NormalX=0 NormalY=0 NormalZ=1 AngleXU=0 Radius=16
  constraints (3):
    c: PointOnObject(g0,g-2)
    c: DistanceY(g0,g-6) = 25
    c: Radius(g0) = 16
FEATURE [PartDesign::Pad] Pad008  label="isb_sensor"
  BaseFeature = -> Pad007
  Length = 16.5
  Length2 = 100
  Placement = pos=(0,0,0) rot=(1,0,0;1.5708rad)
  Profile = -> Sketch012
  Refine = true
  Type = 0
FEATURE [Sketcher::SketchObject] Sketch013  label="isb_spacer_sketch"
  ExternalGeometry = -> [Pad008]
  MapMode = 5
  Placement = pos=(0,0,0) rot=(-1,0,0;1.5708rad)
  Support = -> [Pad008]
  sketch-geometry (8):
    g0: Circle CenterX=-15.95 CenterY=18.7 CenterZ=0 NormalX=0 NormalY=0 NormalZ=1 AngleXU=0 Radius=3
    g1: Circle CenterX=16.05 CenterY=18.7 CenterZ=0 NormalX=0 NormalY=0 NormalZ=1 AngleXU=0 Radius=3
    g2: Circle CenterX=16.05 CenterY=-13.3 CenterZ=0 NormalX=0 NormalY=0 NormalZ=1 AngleXU=0 Radius=3
    g3: Circle CenterX=-15.95 CenterY=-13.3 CenterZ=0 NormalX=0 NormalY=0 NormalZ=1 AngleXU=0 Radius=3
    g4: Circle CenterX=-15.95 CenterY=18.7 CenterZ=0 NormalX=0 NormalY=0 NormalZ=1 AngleXU=0 Radius=1.6
    g5: Circle CenterX=16.05 CenterY=18.7 CenterZ=0 NormalX=0 NormalY=0 NormalZ=1 AngleXU=0 Radius=1.6
    g6: Circle CenterX=-15.95 CenterY=-13.3 CenterZ=0 NormalX=0 NormalY=0 NormalZ=1 AngleXU=0 Radius=1.6
    g7: Circle CenterX=16.05 CenterY=-13.3 CenterZ=0 NormalX=0 NormalY=0 NormalZ=1 AngleXU=0 Radius=1.6
  constraints (16):
    c: Coincident(g0,g-3)
    c: Coincident(g1,g-4)
    c: Coincident(g2,g-5)
    c: Coincident(g3,g-6)
    c: Equal(g0,g3)
    c: Equal(g3,g2)
    c: Equal(g2,g1)
    c: Radius(g0) = 3
    c: Equal(g4,g-3)
    c: Coincident(g4,g0)
    c: Equal(g5,g-4)
    c: Coincident(g5,g1)
    c: Equal(g6,g-6)
    c: Equal(g7,g-5)
    c: Coincident(g7,g2)
    c: Coincident(g6,g3)
FEATURE [PartDesign::Pad] Pad009  label="isb_spacer"
  BaseFeature = -> Pad008
  Length = 4
  Length2 = 100
  Placement = pos=(0,0,0) rot=(1,0,0;1.5708rad)
  Profile = -> Sketch013
  Refine = true
  Type = 0
FEATURE [PartDesign::Chamfer] Chamfer001
  Base = -> Pad009 [Edge31]
  BaseFeature = -> Pad009
  Placement = pos=(0,0,0) rot=(1,0,0;1.5708rad)
  Size = 1
FEATURE [PartDesign::Body] Body008  label="isb"
  Group = -> [Sketch011,Pad007,Sketch012,Pad008,Sketch013,Pad009,Chamfer001]
  Origin = -> Origin008
  Placement = pos=(-20,-18.1,-102.9) rot=(0,0,1;0rad)
  Tip = -> Chamfer001
  expr: Placement.Base.y = -housing_body_sketch.Constraints.housing_depth_front - 5.6mm
FEATURE [Part::FeaturePython] Clone  label="isb001"  # Draft clone (typed FeaturePython)
  AttacherType = Attacher::AttachEngine3D
  Fuse = false
  Objects = -> [Body008]
  Placement = pos=(20,-18.1,-102.9) rot=(0,0,1;0rad)
  Scale = (1,1,1)
  expr: Placement.Base.y = -housing_body_sketch.Constraints.housing_depth_front - 5.6mm
FEATURE [Part::FeaturePython] Clone001  label="isb002"  # Draft clone (typed FeaturePython)
  AttacherType = Attacher::AttachEngine3D
  Fuse = false
  Objects = -> [Clone]
  Placement = pos=(-20,-18.1,-57.5) rot=(0,1,0;3.14159rad)
  Scale = (1,1,1)
  expr: Placement.Base.y = -housing_body_sketch.Constraints.housing_depth_front - 5.6mm
FEATURE [Part::FeaturePython] Clone002  label="isb003"  # Draft clone (typed FeaturePython)
  AttacherType = Attacher::AttachEngine3D
  Fuse = false
  Objects = -> [Clone001]
  Placement = pos=(20,-18.1,-57.5) rot=(0,1,0;3.14159rad)
  Scale = (1,1,1)
  expr: Placement.Base.y = -housing_body_sketch.Constraints.housing_depth_front - 5.6mm
FEATURE [Sketcher::SketchObject] Sketch014  label="housing_platform_sketch"
  MapMode = 5
  Placement = pos=(0,2.13e-14,97) rot=(1,0,0;3.14159rad)
  Support = -> [Pocket002]
  expr: Constraints[8] = fan_body_sketch.Constraints.fan_hole_radius
  expr: Constraints[6] = fan_body_sketch.Constraints.fan_hole_radius
  expr: Constraints[5] = fan_body_sketch.Constraints.hole_center_distance
  expr: Constraints[4] = fan_body_sketch.Constraints.hole_center_distance
  sketch-geometry (4):
    g0: Circle CenterX=-35.3553 CenterY=0 CenterZ=0 NormalX=0 NormalY=0 NormalZ=1 AngleXU=0 Radius=5
    g1: Circle CenterX=35.3553 CenterY=0 CenterZ=0 NormalX=0 NormalY=0 NormalZ=1 AngleXU=0 Radius=5
    g2: Circle CenterX=-35.3553 CenterY=0 CenterZ=0 NormalX=0 NormalY=0 NormalZ=1 AngleXU=0 Radius=2.15
    g3: Circle CenterX=35.3553 CenterY=0 CenterZ=0 NormalX=0 NormalY=0 NormalZ=1 AngleXU=0 Radius=2.15
  constraints (10):
    c: PointOnObject(g0,g-1)
    c: PointOnObject(g1,g-1)
    c: Equal(g0,g1)
    c: Radius(g0) = 5
    c: DistanceX(g0,g-1) = 35.3553
    c: DistanceX(g-1,g1) = 35.3553
    c: Radius(g2) = 2.15
    c: Coincident(g2,g0)
    c: Radius(g3) = 2.15
    c: Coincident(g1,g3)
FEATURE [PartDesign::Pad] Pad010  label="housing_platform"
  BaseFeature = -> Pocket002
  Length = 2.5
  Length2 = 100
  Profile = -> Sketch014
  Refine = true
  Type = 0
FEATURE [Sketcher::SketchObject] Sketch015  label="pmplate_base_sketch"
  MapMode = 5
  Placement = pos=(0,0,0) rot=(1,0,0;1.5708rad)
  Support = -> [XZ_Plane009]
  expr: Constraints[30] = housing_cutouts_sketch.Constraints.housing_hole_radius
  expr: Constraints[22] = housing_cutouts_sketch.Constraints.module_hole_inset
  expr: Constraints[21] = housing_cutouts_sketch.Constraints.module_hole_inset
  expr: Constraints[20] = (housing_body.Length - housing_cutouts_sketch.Constraints.module_height) / 2 + housing_cutouts_sketch.Constraints.module_hole_inset
  expr: Constraints[19] = (housing_body.Length - housing_cutouts_sketch.Constraints.module_height) / 2 + housing_cutouts_sketch.Constraints.module_hole_inset
  expr: Constraints[10] = housing_body.Length
  expr: Constraints[9] = housing_cutouts_sketch.Constraints.module_width
  sketch-geometry (15):
    g0: LineSegment StartX=-45 StartY=-50 StartZ=0 EndX=45 EndY=-50 EndZ=0
    g1: LineSegment StartX=45 StartY=-50 StartZ=0 EndX=45 EndY=50 EndZ=0
    g2: LineSegment StartX=45 StartY=50 StartZ=0 EndX=-45 EndY=50 EndZ=0
    g3: LineSegment StartX=-45 StartY=50 StartZ=0 EndX=-45 EndY=-50 EndZ=0
    g4: LineSegment [constr] StartX=-42 StartY=47 StartZ=0 EndX=42 EndY=47 EndZ=0
    g5: LineSegment [constr] StartX=42 StartY=47 StartZ=0 EndX=42 EndY=-47 EndZ=0
    g6: LineSegment [constr] StartX=42 StartY=-47 StartZ=0 EndX=-42 EndY=-47 EndZ=0
    g7: LineSegment [constr] StartX=-42 StartY=-47 StartZ=0 EndX=-42 EndY=47 EndZ=0
    g8: Circle CenterX=-42 CenterY=47 CenterZ=0 NormalX=0 NormalY=0 NormalZ=1 AngleXU=0 Radius=1.6
    g9: Circle CenterX=42 CenterY=47 CenterZ=0 NormalX=0 NormalY=0 NormalZ=1 AngleXU=0 Radius=1.6
    g10: Circle CenterX=42 CenterY=-47 CenterZ=0 NormalX=0 NormalY=0 NormalZ=1 AngleXU=0 Radius=1.6
    g11: Circle CenterX=-42 CenterY=-47 CenterZ=0 NormalX=0 NormalY=0 NormalZ=1 AngleXU=0 Radius=1.6
    g12: Circle CenterX=-11 CenterY=31 CenterZ=0 NormalX=0 NormalY=0 NormalZ=1 AngleXU=0 Radius=1.6
    g13: Circle CenterX=-30 CenterY=-24 CenterZ=0 NormalX=0 NormalY=0 NormalZ=1 AngleXU=0 Radius=1.6
    g14: Circle CenterX=30 CenterY=-24 CenterZ=0 NormalX=0 NormalY=0 NormalZ=1 AngleXU=0 Radius=1.6
  constraints (40):
    c: Coincident(g0,g1)
    c: Coincident(g1,g2)
    c: Coincident(g2,g3)
    c: Coincident(g3,g0)
    c: Horizontal(g0)
    c: Horizontal(g2)
    c: Vertical(g1)
    c: Vertical(g3)
    c: Symmetric(g0,g1,g-1)
    c: DistanceX(g2,g2) = 90
    c: DistanceY(g1,g1) = 100
    c: Coincident(g4,g5)
    c: Coincident(g5,g6)
    c: Coincident(g6,g7)
    c: Coincident(g7,g4)
    c: Horizontal(g4)
    c: Horizontal(g6)
    c: Vertical(g5)
    c: Vertical(g7)
    c: DistanceY(g4,g2) = 3
    c: DistanceY(g0,g5) = 3
    c: DistanceX(g5,g0) = 3
    c: DistanceX(g2,g4) = 3
    c: Coincident(g8,g4)
    c: Coincident(g9,g4)
    c: Coincident(g10,g5)
    c: Coincident(g11,g6)
    c: Equal(g8,g9)
    c: Equal(g9,g10)
    c: Equal(g10,g11)
    c: Radius(g8) = 1.6
    c: Equal(g12,g13)
    c: Radius(g12) = 1.6
    c: DistanceY(g13,g-1) = 24
    c: DistanceY(g-1,g12) = 31
    c: DistanceX(g12,g-1) = 11
    c: DistanceX(g13,g-1) = 30
    c: Equal(g14,g12)
    c: DistanceX(g-1,g14) = 30
    c: DistanceY(g14,g-1) = 24
FEATURE [PartDesign::Pad] Pad011  label="pmplate_body"
  Length = 1.5
  Length2 = 100
  Placement = pos=(0,0,0) rot=(1,0,0;1.5708rad)
  Profile = -> Sketch015
  Refine = true
  Reversed = true
  Type = 0
FEATURE [PartDesign::Body] Body009  label="pmplate"
  Group = -> [Sketch015,Pad011]
  Origin = -> Origin009
  Placement = pos=(0,15,-80.2) rot=(0,0,1;0rad)
  Tip = -> Pad011
  expr: Placement.Base.y = housing_body_sketch.Constraints.housing_depth_back
FEATURE [Sketcher::SketchObject] Sketch016  label="pm_body_sketch"
  MapMode = 5
  Placement = pos=(0,0,0) rot=(1,0,0;1.5708rad)
  Support = -> [XZ_Plane010]
  sketch-geometry (6):
    g0: LineSegment StartX=-35 StartY=35 StartZ=0 EndX=35 EndY=35 EndZ=0
    g1: LineSegment StartX=35 StartY=35 StartZ=0 EndX=35 EndY=-35 EndZ=0
    g2: LineSegment StartX=35 StartY=-35 StartZ=0 EndX=-35 EndY=-35 EndZ=0
    g3: LineSegment StartX=-35 StartY=-35 StartZ=0 EndX=-35 EndY=35 EndZ=0
    g4: Circle CenterX=-30 CenterY=-24 CenterZ=0 NormalX=0 NormalY=0 NormalZ=1 AngleXU=0 Radius=1.6
    g5: Circle CenterX=-11 CenterY=31 CenterZ=0 NormalX=0 NormalY=0 NormalZ=1 AngleXU=0 Radius=1.6
  constraints (17):
    c: Coincident(g0,g1)
    c: Coincident(g1,g2)
    c: Coincident(g2,g3)
    c: Coincident(g3,g0)
    c: Horizontal(g0)
    c: Horizontal(g2)
    c: Vertical(g1)
    c: Vertical(g3)
    c: Symmetric(g2,g0,g-1)
    c: DistanceX(g0,g0) = 70
    c: DistanceY(g1,g1) = 70
    c: DistanceX(g2,g4) = 5
    c: DistanceY(g2,g4) = 11
    c: Radius(g4) = 1.6
    c: Equal(g4,g5)
    c: DistanceX(g0,g5) = 24
    c: DistanceY(g5,g0) = 4
FEATURE [PartDesign::Pad] Pad012  label="pm_body"
  Length = 5
  Length2 = 100
  Placement = pos=(0,0,0) rot=(1,0,0;1.5708rad)
  Profile = -> Sketch016
  Refine = true
  Reversed = true
  Type = 0
FEATURE [Sketcher::SketchObject] Sketch017  label="pm_plastic_sketch"
  ExternalGeometry = -> [Pad012]
  MapMode = 5
  Placement = pos=(0,5,0) rot=(-1,0,0;1.5708rad)
  Support = -> [Pad012]
  sketch-geometry (9):
    g0: LineSegment StartX=-20 StartY=27 StartZ=0 EndX=-33 EndY=14 EndZ=0
    g1: LineSegment StartX=-33 StartY=14 StartZ=0 EndX=-33 EndY=-8 EndZ=0
    g2: LineSegment StartX=-33 StartY=-8 StartZ=0 EndX=-20 EndY=-8 EndZ=0
    g3: LineSegment StartX=-20 StartY=-8 StartZ=0 EndX=-6 EndY=-32 EndZ=0
    g4: LineSegment StartX=-6 StartY=-32 StartZ=0 EndX=33 EndY=-32 EndZ=0
    g5: LineSegment StartX=33 StartY=-32 StartZ=0 EndX=33 EndY=21 EndZ=0
    g6: LineSegment StartX=33 StartY=21 StartZ=0 EndX=27 EndY=21 EndZ=0
    g7: LineSegment StartX=27 StartY=21 StartZ=0 EndX=27 EndY=27 EndZ=0
    g8: LineSegment StartX=27 StartY=27 StartZ=0 EndX=-20 EndY=27 EndZ=0
  constraints (27):
    c: Coincident(g0,g1)
    c: Vertical(g1)
    c: Coincident(g1,g2)
    c: Horizontal(g2)
    c: Coincident(g2,g3)
    c: Coincident(g3,g4)
    c: Horizontal(g4)
    c: Coincident(g4,g5)
    c: Vertical(g5)
    c: Coincident(g5,g6)
    c: Horizontal(g6)
    c: Coincident(g6,g7)
    c: Vertical(g7)
    c: Coincident(g7,g8)
    c: Coincident(g8,g0)
    c: Horizontal(g8)
    c: DistanceX(g-4,g0) = 2
    c: DistanceX(g5,g-6) = 2
    c: DistanceX(g7,g-6) = 8
    c: DistanceX(g-4,g0) = 15
    c: DistanceY(g0,g-4) = 8
    c: DistanceY(g5,g-6) = 14
    c: DistanceY(g-6,g4) = 3
    c: DistanceY(g-5,g1) = 27
    c: DistanceY(g0,g-4) = 21
    c: DistanceX(g-5,g2) = 15
    c: DistanceX(g-5,g3) = 29
FEATURE [PartDesign::Pad] Pad013  label="pm_plastic"
  BaseFeature = -> Pad012
  Length = 12
  Length2 = 100
  Placement = pos=(0,0,0) rot=(1,0,0;1.5708rad)
  Profile = -> Sketch017
  Refine = true
  Type = 0
FEATURE [Sketcher::SketchObject] Sketch018  label="pm_fan_sketch"
  ExternalGeometry = -> [Pad013]
  MapMode = 5
  Placement = pos=(0,17,0) rot=(-1,0,0;1.5708rad)
  Support = -> [Pad013]
  sketch-geometry (4):
    g0: LineSegment StartX=-4.5 StartY=5 StartZ=0 EndX=30.5 EndY=5 EndZ=0
    g1: LineSegment StartX=30.5 StartY=5 StartZ=0 EndX=30.5 EndY=-30 EndZ=0
    g2: LineSegment StartX=30.5 StartY=-30 StartZ=0 EndX=-4.5 EndY=-30 EndZ=0
    g3: LineSegment StartX=-4.5 StartY=-30 StartZ=0 EndX=-4.5 EndY=5 EndZ=0
  constraints (12):
    c: Coincident(g0,g1)
    c: Coincident(g1,g2)
    c: Coincident(g2,g3)
    c: Coincident(g3,g0)
    c: Horizontal(g0)
    c: Horizontal(g2)
    c: Vertical(g1)
    c: Vertical(g3)
    c: Equal(g1,g2)
    c: DistanceX(g1,g-4) = 2.5
    c: DistanceY(g-4,g1) = 2
    c: DistanceY(g3,g3) = 35
FEATURE [PartDesign::Pad] Pad014  label="pm_fan"
  BaseFeature = -> Pad013
  Length = 7.5
  Length2 = 100
  Placement = pos=(0,0,0) rot=(1,0,0;1.5708rad)
  Profile = -> Sketch018
  Refine = true
  Type = 0
FEATURE [PartDesign::Body] Body010  label="pm"
  Group = -> [Sketch016,Pad012,Sketch017,Pad013,Sketch018,Pad014]
  Origin = -> Origin010
  Placement = pos=(0,16.5,-80.2) rot=(0,0,1;0rad)
  Tip = -> Pad014
  expr: Placement.Base.y = housing_body_sketch.Constraints.housing_depth_back + pmplate_body.Length
FEATURE [Sketcher::SketchObject] Sketch019  label="housing_pmcable_sketch"
  ExternalGeometry = -> [Pad010]
  MapMode = 5
  Placement = pos=(0,15,0) rot=(0,0.707107,0.707107;3.14159rad)
  Support = -> [Pad010]
  sketch-geometry (4):
    g0: LineSegment StartX=17 StartY=100 StartZ=0 EndX=-39.5404 EndY=100 EndZ=0
    g1: LineSegment StartX=-39.5404 StartY=100 StartZ=0 EndX=-39.5404 EndY=94.51 EndZ=0
    g2: LineSegment StartX=-39.5404 StartY=94.51 StartZ=0 EndX=17 EndY=94.51 EndZ=0
    g3: LineSegment StartX=17 StartY=94.51 StartZ=0 EndX=17 EndY=100 EndZ=0
  constraints (12):
    c: Coincident(g0,g1)
    c: Coincident(g1,g2)
    c: Coincident(g2,g3)
    c: Coincident(g3,g0)
    c: Horizontal(g0)
    c: Horizontal(g2)
    c: Vertical(g1)
    c: Vertical(g3)
    c: PointOnObject(g0,g-3)
    c: PointOnObject(g1,g-4)
    c: DistanceX(g1,g-5) = 10
    c: DistanceX(g2,g-5) = 25
FEATURE [PartDesign::Pocket] Pocket  label="housing_pmcable"
  BaseFeature = -> Pad010
  Length = 1.5
  Length2 = 100
  Profile = -> Sketch019
  Refine = true
  Type = 0
FEATURE [Part::FeaturePython] Screw004  label="M3x30-Screw"  # Fasteners workbench fastener (typed FeaturePython)
  Placement = pos=(42,-14.1,-33.2) rot=(1,0,0;1.5708rad)
  diameter = 4
  invert = false
  length = 10
  matchOuter = false
  offset = 0
  thread = false
  type = 16
FEATURE [Sketcher::SketchObject] Sketch020  label="housing_power_sketch"
  MapMode = 5
  Placement = pos=(0,0,0) rot=(1,0,0;3.14159rad)
  Support = -> [Pocket]
  sketch-geometry (1):
    g0: Circle CenterX=0 CenterY=0 CenterZ=0 NormalX=0 NormalY=0 NormalZ=1 AngleXU=0 Radius=5.7
  constraints (2):
    c: Coincident(g0,g-1)
    c: Diameter(g0) = 11.4
FEATURE [PartDesign::Pocket] Pocket004  label="housing_power_hole"
  BaseFeature = -> Pocket
  Length = 10
  Length2 = 100
  Profile = -> Sketch020
  Refine = true
  Type = 0
FEATURE [PartDesign::Body] Body006  label="housing"
  Group = -> [Sketch006,Pad005,Sketch007,Pocket001,Sketch008,Pocket002,Sketch014,Pad010,Sketch019,Pocket,Sketch020,Pocket004]
  Origin = -> Origin006
  Placement = pos=(0,0,-130.2) rot=(0,0,1;0rad)
  Tip = -> Pocket004
FEATURE [Mesh::Feature] Mesh  label="housing (Meshed)"
FEATURE [Mesh::Feature] Mesh001  label="pmplate (Meshed)"
FEATURE [Mesh::Feature] Mesh002  label="cross (Meshed)"
FEATURE [Mesh::Feature] Mesh003  label="plate (Meshed)"
